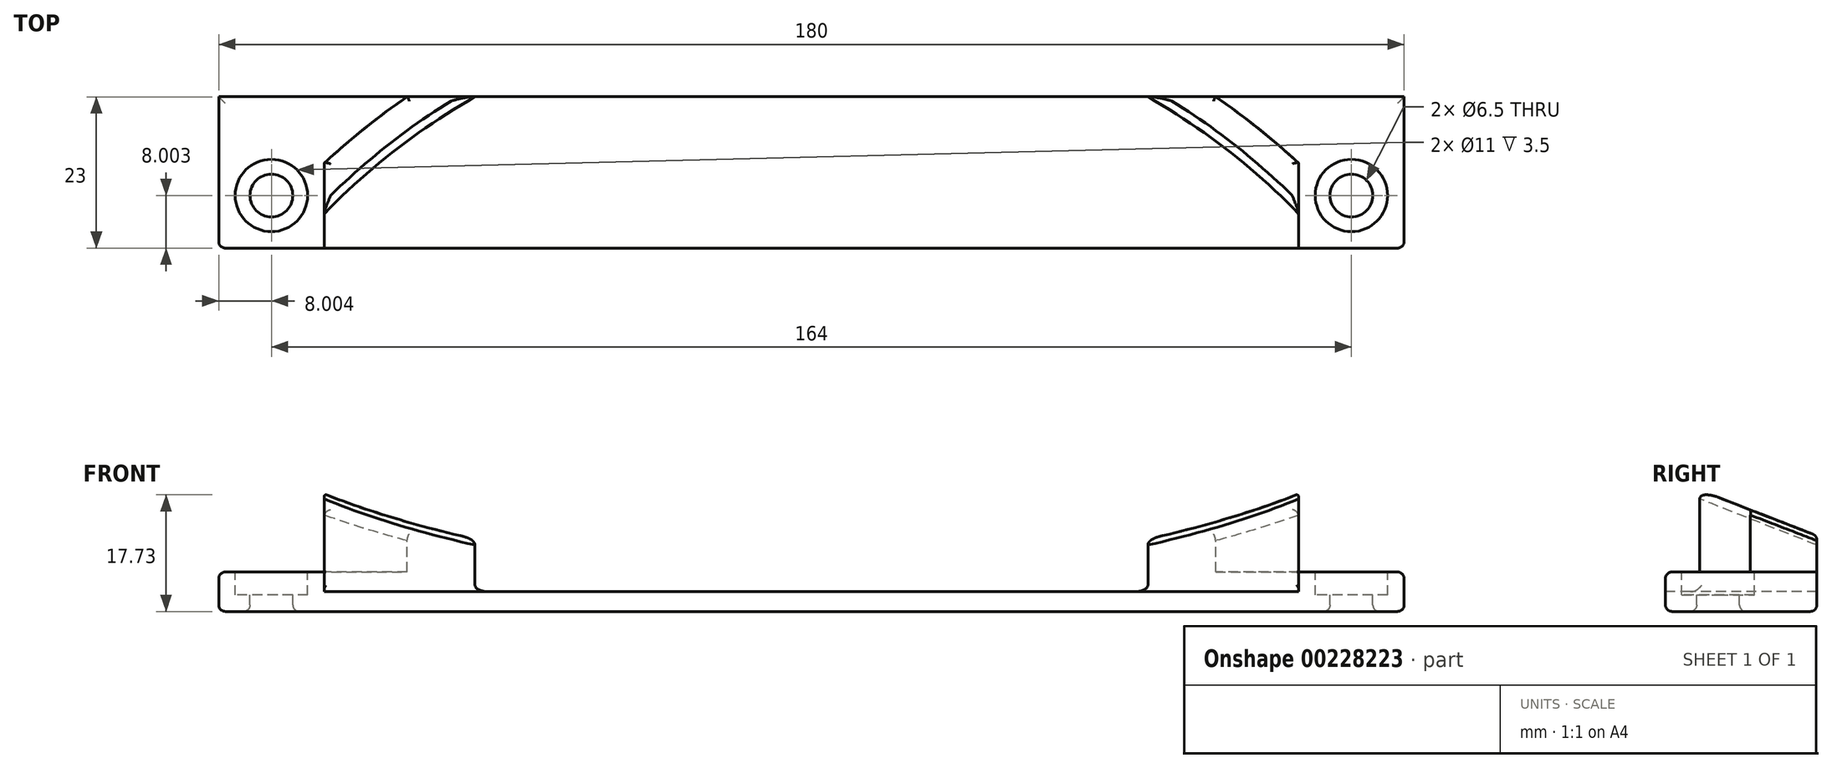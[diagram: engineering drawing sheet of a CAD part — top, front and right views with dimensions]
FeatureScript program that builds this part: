
annotation { "Feature Type Name" : "Feature", "Feature Type Description" : "" }
export const myFeature = defineFeature(function(context is Context, id is Id, definition is map)
    precondition{}
    {
        {
            var Q0;
            Q0=qCreatedBy(makeId("Top.planeOp"),FACE);
            var sketch = newSketch(context, id + "F0", { "sketchPlane" : qUnion([Q0])});
            skLineSegment(sketch, "E0.bottom", {"start": v(-72.48, -7.14) * mm, "end": v(107.52, -7.14) * mm});
            skLineSegment(sketch, "E0.top", {"start": v(-72.48, -30.14) * mm, "end": v(107.52, -30.14) * mm});
            skLineSegment(sketch, "E0.left", {"start": v(-72.48, -7.14) * mm, "end": v(-72.48, -30.14) * mm});
            skLineSegment(sketch, "E0.right", {"start": v(107.52, -7.14) * mm, "end": v(107.52, -30.14) * mm});
            skPoint(sketch, "E1", {"position": v(-64.48, -22.14) * mm});
            skPoint(sketch, "E2", {"position": v(99.52, -22.14) * mm});
            skSolve(sketch);
        }
        {
            var Q0;
            Q0=makeQuery(id+"F0.imprint","IMPRINT",FACE,{"disambiguationData":[TD([[makeQuery(id+"F0.imprint","IMPRINT",EDGE,{"derivedFrom":sQuery(id+"F0.wireOp",EDGE,"E0.bottom")}),-1.0]])]});
            extrude(context, id + "F1", {"entities" : qUnion([Q0]), "depth" : 6 * mm});
        }
        {
            var Q0;
            Q0=makeQuery(id+"F1.opExtrude","CAP_FACE",FACE,{"disambiguationData":[OSD([sQuery(id+"F0.wireOp",EDGE,"E0.bottom"),sQuery(id+"F0.wireOp",EDGE,"E0.top"),sQuery(id+"F0.wireOp",EDGE,"E0.left"),sQuery(id+"F0.wireOp",EDGE,"E0.right")])],"isStart":false});
            var sketch = newSketch(context, id + "F2", { "sketchPlane" : qUnion([Q0])});
            skPoint(sketch, "E3", {"position": v(-64.48, -22.14) * mm});
            skPoint(sketch, "E4", {"position": v(99.52, -22.14) * mm});
            skLineSegment(sketch, "E5.bottom", {"start": v(-56.48, -7.14) * mm, "end": v(91.52, -7.14) * mm});
            skLineSegment(sketch, "E5.top", {"start": v(-56.48, -30.14) * mm, "end": v(91.52, -30.14) * mm});
            skLineSegment(sketch, "E5.left", {"start": v(-56.48, -7.14) * mm, "end": v(-56.48, -30.14) * mm});
            skLineSegment(sketch, "E5.right", {"start": v(91.52, -7.14) * mm, "end": v(91.52, -30.14) * mm});
            skSolve(sketch);
        }
        {
            var Q0;
            Q0=sQuery(id+"F2.wireOp",VERTEX,"E3");
            var Q1;
            Q1=sQuery(id+"F2.wireOp",VERTEX,"E4");
            var Q2;
            Q2=makeQuery(id+"F1.opExtrude","SWEPT_BODY",BODY,{"disambiguationData":[OSD([sQuery(id+"F0.wireOp",EDGE,"E0.bottom"),sQuery(id+"F0.wireOp",EDGE,"E0.top"),sQuery(id+"F0.wireOp",EDGE,"E0.left"),sQuery(id+"F0.wireOp",EDGE,"E0.right")])]});
            hole(context, id + "F3", {"style" : HoleStyle.C_BORE, "endStyle" : HoleEndStyle.THROUGH, "holeDiameter" : 6.5 * mm, "cBoreDiameter" : 11 * mm, "cBoreDepth" : 3.5 * mm, "startFromSketch" : true, "locations" : qUnion([Q0, Q1]), "scope" : qUnion([Q2]), "isTappedThrough" : true});
        }
        {
            var Q0;
            Q0=makeQuery(id+"F2.imprint","IMPRINT",FACE,{"disambiguationData":[TD([[makeQuery(id+"F2.imprint","IMPRINT",EDGE,{"derivedFrom":sQuery(id+"F2.wireOp",EDGE,"E5.bottom")}),-1.0]])]});
            extrude(context, id + "F4", {"entities" : qUnion([Q0]), "operationType" : NewBodyOperationType.ADD, "depth" : 14 * mm});
        }
        {
            var Q0;
            Q0=makeQuery(id+"F4.opExtrude","CAP_FACE",FACE,{"disambiguationData":[OSD([sQuery(id+"F2.wireOp",EDGE,"E5.bottom"),sQuery(id+"F2.wireOp",EDGE,"E5.top"),sQuery(id+"F2.wireOp",EDGE,"E5.left"),sQuery(id+"F2.wireOp",EDGE,"E5.right")])],"isStart":false});
            var sketch = newSketch(context, id + "F5", { "sketchPlane" : qUnion([Q0])});
            skPoint(sketch, "E6", {"position": v(17.52, 2.86) * mm});
            skCircle(sketch, "E7", {"center": v(17.52, -96.6) * mm, "radius": 108.5 * mm});
            skCircle(sketch, "E8", {"center": v(17.52, -96.6) * mm, "radius": 103.03 * mm});
            skSolve(sketch);
        }
        {
            var Q0;
            {var subQ1=makeQuery(id+"F4.opExtrude","CAP_EDGE",EDGE,{"disambiguationData":[OSD([sQuery(id+"F2.wireOp",EDGE,"E5.top")])],"isStart":false});Q0=makeQuery(id+"F5.imprint","IMPRINT",FACE,{"disambiguationData":[TD([[makeQuery(id+"F5.imprint","IMPRINT",EDGE,{"derivedFrom":subQ1}),1.0]])]});}
            extrude(context, id + "F6", {"entities" : qUnion([Q0]), "operationType" : NewBodyOperationType.REMOVE, "oppositeDirection" : true, "depth" : 17 * mm});
        }
        {
            var Q0;
            {var subQ0=sQuery(id+"F5.wireOp",EDGE,"E7");var subQ1=makeQuery(id+"F4.opExtrude","CAP_EDGE",EDGE,{"disambiguationData":[OSD([sQuery(id+"F2.wireOp",EDGE,"E5.bottom")])],"isStart":false});var subQ2=makeQuery(id+"F5.imprint","INTERSECT",VERTEX,{"disambiguationData":[OD(1.0)],"derivedFrom":[subQ1,subQ0]});Q0=makeQuery(id+"F5.imprint","IMPRINT",FACE,{"disambiguationData":[TD([[makeQuery(id+"F5.imprint","IMPRINT",EDGE,{"disambiguationData":[TD([[subQ2,-1.0]])],"derivedFrom":subQ0}),-1.0]])]});}
            var Q1;
            {var subQ0=sQuery(id+"F5.wireOp",EDGE,"E7");var subQ1=makeQuery(id+"F4.opExtrude","CAP_EDGE",EDGE,{"disambiguationData":[OSD([sQuery(id+"F2.wireOp",EDGE,"E5.bottom")])],"isStart":false});var subQ2=makeQuery(id+"F5.imprint","INTERSECT",VERTEX,{"disambiguationData":[OD(0.0)],"derivedFrom":[subQ1,subQ0]});Q1=makeQuery(id+"F5.imprint","IMPRINT",FACE,{"disambiguationData":[TD([[makeQuery(id+"F5.imprint","IMPRINT",EDGE,{"disambiguationData":[TD([[subQ2,1.0]])],"derivedFrom":subQ0}),-1.0]])]});}
            extrude(context, id + "F7", {"entities" : qUnion([Q0, Q1]), "operationType" : NewBodyOperationType.REMOVE, "oppositeDirection" : true, "depth" : 14 * mm});
        }
        {
            var Q0;
            Q0=makeQuery(id+"F1.opExtrude","SWEPT_FACE",FACE,{"disambiguationData":[OSD([sQuery(id+"F0.wireOp",EDGE,"E0.right")])]});
            var sketch = newSketch(context, id + "F8", { "sketchPlane" : qUnion([Q0])});
            skLineSegment(sketch, "E9", {"start": v(-29.85, 20.35) * mm, "end": v(-5.4, 10.83) * mm});
            skLineSegment(sketch, "E10", {"start": v(-5.4, 10.83) * mm, "end": v(-5.4, 21.47) * mm});
            skLineSegment(sketch, "E11", {"start": v(-5.4, 21.47) * mm, "end": v(-29.85, 20.35) * mm});
            skSolve(sketch);
        }
        {
            var Q0;
            Q0=makeQuery(id+"F8.imprint","IMPRINT",FACE,{"disambiguationData":[TD([[makeQuery(id+"F8.imprint","IMPRINT",EDGE,{"derivedFrom":sQuery(id+"F8.wireOp",EDGE,"E9")}),1.0]])]});
            extrude(context, id + "F9", {"entities" : qUnion([Q0]), "operationType" : NewBodyOperationType.REMOVE, "oppositeDirection" : true, "depth" : 200 * mm});
        }
        {
            var Q0;
            {var subQ0=sQuery(id+"F2.wireOp",EDGE,"E5.right");Q0=makeQuery(id+"F9.boolean.opBoolean","COPY",FACE,{"disambiguationData":[TD([makeQuery(id+"F4.opExtrude","SWEPT_FACE",FACE,{"disambiguationData":[OSD([subQ0])]})])],"derivedFrom":makeQuery(id+"F9.opExtrude","SWEPT_FACE",FACE,{"disambiguationData":[OSD([sQuery(id+"F25IUwD2cY2oAvL_1.wireOp",EDGE,"SbL0lGDD-A6Ls-py6w-HqPT-BCFnm7Rx5yUF")])]})});}
            var Q1;
            {var subQ0=sQuery(id+"F2.wireOp",EDGE,"E5.left");Q1=makeQuery(id+"F9.boolean.opBoolean","COPY",FACE,{"disambiguationData":[TD([makeQuery(id+"F4.opExtrude","SWEPT_FACE",FACE,{"disambiguationData":[OSD([subQ0])]})])],"derivedFrom":makeQuery(id+"F9.opExtrude","SWEPT_FACE",FACE,{"disambiguationData":[OSD([sQuery(id+"F25IUwD2cY2oAvL_1.wireOp",EDGE,"SbL0lGDD-A6Ls-py6w-HqPT-BCFnm7Rx5yUF")])]})});}
            var Q2;
            Q2=makeQuery(id+"F6.boolean.opBoolean","COPY",EDGE,{"derivedFrom":makeQuery(id+"F6.opExtrude","CAP_EDGE",EDGE,{"disambiguationData":[OSD([sQuery(id+"F2.wireOp",EDGE,"E5.bottom")])],"isStart":false})});
            var Q3;
            Q3=makeQuery(id+"F6.boolean.opBoolean","COPY",EDGE,{"derivedFrom":makeQuery(id+"F6.opExtrude","CAP_EDGE",EDGE,{"disambiguationData":[OSD([sQuery(id+"F2.wireOp",EDGE,"E5.top")])],"isStart":false})});
            var Q4;
            {var subQ0=sQuery(id+"F0.wireOp",EDGE,"E0.right");var subQ1=sQuery(id+"F0.wireOp",EDGE,"E0.top");Q4=makeQuery(id+"F4.boolean.opBoolean","SPLIT",EDGE,{"disambiguationData":[TD([makeQuery(id+"F1.opExtrude","SWEPT_FACE",FACE,{"disambiguationData":[OSD([subQ0])]})])],"derivedFrom":makeQuery(id+"F1.opExtrude","CAP_EDGE",EDGE,{"disambiguationData":[OSD([subQ1])],"isStart":false})});}
            var Q5;
            Q5=makeQuery(id+"F1.opExtrude","CAP_EDGE",EDGE,{"disambiguationData":[OSD([sQuery(id+"F0.wireOp",EDGE,"E0.right")])],"isStart":false});
            var Q6;
            {var subQ0=sQuery(id+"F2.wireOp",EDGE,"E5.right");var subQ1=sQuery(id+"F2.wireOp",EDGE,"E5.bottom");var subQ2=makeQuery(id+"F4.opExtrude","CAP_EDGE",EDGE,{"disambiguationData":[OSD([subQ1])],"isStart":false});var subQ3=sQuery(id+"F0.wireOp",EDGE,"E0.right");var subQ4=sQuery(id+"F0.wireOp",EDGE,"E0.bottom");Q6=makeQuery(id+"F7.boolean.opBoolean","MERGE",EDGE,{"derivedFrom":[makeQuery(id+"F4.boolean.opBoolean","SPLIT",EDGE,{"disambiguationData":[TD([makeQuery(id+"F1.opExtrude","SWEPT_FACE",FACE,{"disambiguationData":[OSD([subQ3])]})])],"derivedFrom":makeQuery(id+"F1.opExtrude","CAP_EDGE",EDGE,{"disambiguationData":[OSD([subQ4])],"isStart":false})}),makeQuery(id+"F7.opExtrude","CAP_EDGE",EDGE,{"disambiguationData":[OSD([subQ1]),TDD([makeQuery(id+"F5.imprint","IMPRINT",EDGE,{"disambiguationData":[TD([[makeQuery(id+"F5.imprint","INTERSECT",VERTEX,{"derivedFrom":[subQ2,makeQuery(id+"F4.opExtrude","CAP_EDGE",EDGE,{"disambiguationData":[OSD([subQ0])],"isStart":false})]}),1.0]])],"derivedFrom":subQ2})])],"isStart":false})]});}
            var Q7;
            Q7=makeQuery(id+"F3.hole-1.boolean.opBoolean","COPY",EDGE,{"derivedFrom":makeQuery(id+"F3.hole-1.opRevolve","SWEPT_EDGE",EDGE,{"disambiguationData":[OSD([sQuery(id+"F3.hole-1.sketch.wireOp",EDGE,"cbore_start_line_2"),sQuery(id+"F3.hole-1.sketch.wireOp",EDGE,"cbore_start_line_3")])]})});
            var Q8;
            Q8=makeQuery(id+"F3.hole-1.boolean.opBoolean","COPY",EDGE,{"derivedFrom":makeQuery(id+"F3.hole-1.opRevolve","SWEPT_EDGE",EDGE,{"disambiguationData":[OSD([sQuery(id+"F3.hole-1.sketch.wireOp",EDGE,"cbore_start_line_1"),sQuery(id+"F3.hole-1.sketch.wireOp",EDGE,"core_line_2")])]})});
            var Q9;
            Q9=makeQuery(id+"F3.hole-0.boolean.opBoolean","COPY",EDGE,{"derivedFrom":makeQuery(id+"F3.hole-0.opRevolve","SWEPT_EDGE",EDGE,{"disambiguationData":[OSD([sQuery(id+"F3.hole-0.sketch.wireOp",EDGE,"cbore_start_line_1"),sQuery(id+"F3.hole-0.sketch.wireOp",EDGE,"core_line_2")])]})});
            var Q10;
            Q10=makeQuery(id+"F3.hole-0.boolean.opBoolean","COPY",EDGE,{"derivedFrom":makeQuery(id+"F3.hole-0.opRevolve","SWEPT_EDGE",EDGE,{"disambiguationData":[OSD([sQuery(id+"F3.hole-0.sketch.wireOp",EDGE,"cbore_start_line_2"),sQuery(id+"F3.hole-0.sketch.wireOp",EDGE,"cbore_start_line_3")])]})});
            var Q11;
            {var subQ0=sQuery(id+"F0.wireOp",EDGE,"E0.left");var subQ1=sQuery(id+"F0.wireOp",EDGE,"E0.top");Q11=makeQuery(id+"F4.boolean.opBoolean","SPLIT",EDGE,{"disambiguationData":[TD([makeQuery(id+"F1.opExtrude","SWEPT_FACE",FACE,{"disambiguationData":[OSD([subQ0])]})])],"derivedFrom":makeQuery(id+"F1.opExtrude","CAP_EDGE",EDGE,{"disambiguationData":[OSD([subQ1])],"isStart":false})});}
            var Q12;
            Q12=makeQuery(id+"F1.opExtrude","CAP_EDGE",EDGE,{"disambiguationData":[OSD([sQuery(id+"F0.wireOp",EDGE,"E0.left")])],"isStart":false});
            var Q13;
            {var subQ0=sQuery(id+"F2.wireOp",EDGE,"E5.left");var subQ1=sQuery(id+"F2.wireOp",EDGE,"E5.bottom");var subQ2=makeQuery(id+"F4.opExtrude","CAP_EDGE",EDGE,{"disambiguationData":[OSD([subQ1])],"isStart":false});var subQ3=sQuery(id+"F0.wireOp",EDGE,"E0.left");var subQ4=sQuery(id+"F0.wireOp",EDGE,"E0.bottom");Q13=makeQuery(id+"F7.boolean.opBoolean","MERGE",EDGE,{"derivedFrom":[makeQuery(id+"F4.boolean.opBoolean","SPLIT",EDGE,{"disambiguationData":[TD([makeQuery(id+"F1.opExtrude","SWEPT_FACE",FACE,{"disambiguationData":[OSD([subQ3])]})])],"derivedFrom":makeQuery(id+"F1.opExtrude","CAP_EDGE",EDGE,{"disambiguationData":[OSD([subQ4])],"isStart":false})}),makeQuery(id+"F7.opExtrude","CAP_EDGE",EDGE,{"disambiguationData":[OSD([subQ1]),TDD([makeQuery(id+"F5.imprint","IMPRINT",EDGE,{"disambiguationData":[TD([[makeQuery(id+"F5.imprint","INTERSECT",VERTEX,{"derivedFrom":[subQ2,makeQuery(id+"F4.opExtrude","CAP_EDGE",EDGE,{"disambiguationData":[OSD([subQ0])],"isStart":false})]}),-1.0]])],"derivedFrom":subQ2})])],"isStart":false})]});}
            var Q14;
            Q14=makeQuery(id+"F1.opExtrude","CAP_EDGE",EDGE,{"disambiguationData":[OSD([sQuery(id+"F0.wireOp",EDGE,"E0.bottom")])],"isStart":true});
            var Q15;
            Q15=makeQuery(id+"F1.opExtrude","CAP_EDGE",EDGE,{"disambiguationData":[OSD([sQuery(id+"F0.wireOp",EDGE,"E0.top")])],"isStart":true});
            var Q16;
            Q16=makeQuery(id+"F1.opExtrude","CAP_EDGE",EDGE,{"disambiguationData":[OSD([sQuery(id+"F0.wireOp",EDGE,"E0.right")])],"isStart":true});
            var Q17;
            Q17=makeQuery(id+"F1.opExtrude","CAP_EDGE",EDGE,{"disambiguationData":[OSD([sQuery(id+"F0.wireOp",EDGE,"E0.left")])],"isStart":true});
            var Q18;
            Q18=makeQuery(id+"F1.opExtrude","CAP_FACE",FACE,{"disambiguationData":[OSD([sQuery(id+"F0.wireOp",EDGE,"E0.bottom"),sQuery(id+"F0.wireOp",EDGE,"E0.top"),sQuery(id+"F0.wireOp",EDGE,"E0.left"),sQuery(id+"F0.wireOp",EDGE,"E0.right")])],"isStart":true});
            var Q19;
            Q19=makeQuery(id+"F3.hole-0.boolean.opBoolean","INTERSECT",EDGE,{"derivedFrom":[makeQuery(id+"F1.opExtrude","CAP_FACE",FACE,{"disambiguationData":[OSD([sQuery(id+"F0.wireOp",EDGE,"E0.bottom"),sQuery(id+"F0.wireOp",EDGE,"E0.top"),sQuery(id+"F0.wireOp",EDGE,"E0.left"),sQuery(id+"F0.wireOp",EDGE,"E0.right")])],"isStart":true}),makeQuery(id+"F3.hole-0.opRevolve","SWEPT_FACE",FACE,{"disambiguationData":[OSD([sQuery(id+"F3.hole-0.sketch.wireOp",EDGE,"core_line_2")])]})]});
            var Q20;
            Q20=makeQuery(id+"F7.boolean.opBoolean","COPY",EDGE,{"derivedFrom":makeQuery(id+"F7.opExtrude","SWEPT_EDGE",EDGE,{"disambiguationData":[OSD([sQuery(id+"F2.wireOp",EDGE,"E5.left"),sQuery(id+"F5.wireOp",EDGE,"E7")])]})});
            var Q21;
            {var subQ0=sQuery(id+"F5.wireOp",EDGE,"E7");var subQ1=sQuery(id+"F2.wireOp",EDGE,"E5.bottom");Q21=makeQuery(id+"F7.boolean.opBoolean","COPY",EDGE,{"derivedFrom":makeQuery(id+"F7.opExtrude","SWEPT_EDGE",EDGE,{"disambiguationData":[OSD([subQ1,subQ0]),TDD([makeQuery(id+"F5.imprint","INTERSECT",VERTEX,{"disambiguationData":[OD(1.0)],"derivedFrom":[makeQuery(id+"F4.opExtrude","CAP_EDGE",EDGE,{"disambiguationData":[OSD([subQ1])],"isStart":false}),subQ0]})])]})});}
            var Q22;
            Q22=makeQuery(id+"F7.boolean.opBoolean","COPY",EDGE,{"derivedFrom":makeQuery(id+"F7.opExtrude","SWEPT_EDGE",EDGE,{"disambiguationData":[OSD([sQuery(id+"F2.wireOp",EDGE,"E5.right"),sQuery(id+"F5.wireOp",EDGE,"E7")])]})});
            var Q23;
            {var subQ0=sQuery(id+"F5.wireOp",EDGE,"E8");Q23=makeQuery(id+"F9.boolean.opBoolean","INTERSECT",EDGE,{"derivedFrom":[makeQuery(id+"F6.boolean.opBoolean","COPY",FACE,{"derivedFrom":makeQuery(id+"F6.opExtrude","SWEPT_FACE",FACE,{"disambiguationData":[OSD([subQ0]),TDD([makeQuery(id+"F5.imprint","IMPRINT",EDGE,{"disambiguationData":[TD([[makeQuery(id+"F5.imprint","INTERSECT",VERTEX,{"disambiguationData":[OD(0.0)],"derivedFrom":[makeQuery(id+"F4.opExtrude","CAP_EDGE",EDGE,{"disambiguationData":[OSD([sQuery(id+"F2.wireOp",EDGE,"E5.bottom")])],"isStart":false}),subQ0]}),1.0]])],"derivedFrom":subQ0})])]})}),makeQuery(id+"F9.opExtrude","SWEPT_FACE",FACE,{"disambiguationData":[OSD([sQuery(id+"F8.wireOp",EDGE,"E9")])]})]});}
            var Q24;
            {var subQ0=sQuery(id+"F5.wireOp",EDGE,"E7");Q24=makeQuery(id+"F9.boolean.opBoolean","INTERSECT",EDGE,{"derivedFrom":[makeQuery(id+"F7.boolean.opBoolean","COPY",FACE,{"derivedFrom":makeQuery(id+"F7.opExtrude","SWEPT_FACE",FACE,{"disambiguationData":[OSD([subQ0]),TDD([makeQuery(id+"F5.imprint","IMPRINT",EDGE,{"disambiguationData":[TD([[makeQuery(id+"F5.imprint","INTERSECT",VERTEX,{"disambiguationData":[OD(0.0)],"derivedFrom":[makeQuery(id+"F4.opExtrude","CAP_EDGE",EDGE,{"disambiguationData":[OSD([sQuery(id+"F2.wireOp",EDGE,"E5.bottom")])],"isStart":false}),subQ0]}),1.0]])],"derivedFrom":subQ0})])]})}),makeQuery(id+"F9.opExtrude","SWEPT_FACE",FACE,{"disambiguationData":[OSD([sQuery(id+"F8.wireOp",EDGE,"E9")])]})]});}
            var Q25;
            Q25=makeQuery(id+"F9.boolean.opBoolean","INTERSECT",EDGE,{"disambiguationData":[OD(0.0)],"derivedFrom":[makeQuery(id+"F4.boolean.opBoolean","MERGE",FACE,{"derivedFrom":[makeQuery(id+"F1.opExtrude","SWEPT_FACE",FACE,{"disambiguationData":[OSD([sQuery(id+"F0.wireOp",EDGE,"E0.bottom")])]}),makeQuery(id+"F4.opExtrude","SWEPT_FACE",FACE,{"disambiguationData":[OSD([sQuery(id+"F2.wireOp",EDGE,"E5.bottom")])]})]}),makeQuery(id+"F9.opExtrude","SWEPT_FACE",FACE,{"disambiguationData":[OSD([sQuery(id+"F8.wireOp",EDGE,"E9")])]})]});
            var Q26;
            Q26=makeQuery(id+"F9.boolean.opBoolean","INTERSECT",EDGE,{"derivedFrom":[makeQuery(id+"F4.opExtrude","SWEPT_FACE",FACE,{"disambiguationData":[OSD([sQuery(id+"F2.wireOp",EDGE,"E5.right")])]}),makeQuery(id+"F9.opExtrude","SWEPT_FACE",FACE,{"disambiguationData":[OSD([sQuery(id+"F8.wireOp",EDGE,"E9")])]})]});
            var Q27;
            {var subQ0=sQuery(id+"F2.wireOp",EDGE,"E5.right");var subQ1=sQuery(id+"F2.wireOp",EDGE,"E5.bottom");var subQ2=sQuery(id+"F5.wireOp",EDGE,"E8");Q27=makeQuery(id+"F6.boolean.opBoolean","COPY",EDGE,{"disambiguationData":[TD([makeQuery(id+"F4.opExtrude","CAP_FACE",FACE,{"disambiguationData":[OSD([subQ1,sQuery(id+"F2.wireOp",EDGE,"E5.top"),sQuery(id+"F2.wireOp",EDGE,"E5.left"),subQ0])],"isStart":false})])],"derivedFrom":makeQuery(id+"F6.opExtrude","SWEPT_EDGE",EDGE,{"disambiguationData":[OSD([subQ0,subQ2])]})});}
            var Q28;
            {var subQ0=sQuery(id+"F5.wireOp",EDGE,"E7");Q28=makeQuery(id+"F9.boolean.opBoolean","INTERSECT",EDGE,{"derivedFrom":[makeQuery(id+"F7.boolean.opBoolean","COPY",FACE,{"derivedFrom":makeQuery(id+"F7.opExtrude","SWEPT_FACE",FACE,{"disambiguationData":[OSD([subQ0]),TDD([makeQuery(id+"F5.imprint","IMPRINT",EDGE,{"disambiguationData":[TD([[makeQuery(id+"F5.imprint","INTERSECT",VERTEX,{"disambiguationData":[OD(1.0)],"derivedFrom":[makeQuery(id+"F4.opExtrude","CAP_EDGE",EDGE,{"disambiguationData":[OSD([sQuery(id+"F2.wireOp",EDGE,"E5.bottom")])],"isStart":false}),subQ0]}),-1.0]])],"derivedFrom":subQ0})])]})}),makeQuery(id+"F9.opExtrude","SWEPT_FACE",FACE,{"disambiguationData":[OSD([sQuery(id+"F8.wireOp",EDGE,"E9")])]})]});}
            var Q29;
            Q29=makeQuery(id+"F9.boolean.opBoolean","INTERSECT",EDGE,{"disambiguationData":[OD(1.0)],"derivedFrom":[makeQuery(id+"F4.boolean.opBoolean","MERGE",FACE,{"derivedFrom":[makeQuery(id+"F1.opExtrude","SWEPT_FACE",FACE,{"disambiguationData":[OSD([sQuery(id+"F0.wireOp",EDGE,"E0.bottom")])]}),makeQuery(id+"F4.opExtrude","SWEPT_FACE",FACE,{"disambiguationData":[OSD([sQuery(id+"F2.wireOp",EDGE,"E5.bottom")])]})]}),makeQuery(id+"F9.opExtrude","SWEPT_FACE",FACE,{"disambiguationData":[OSD([sQuery(id+"F8.wireOp",EDGE,"E9")])]})]});
            var Q30;
            Q30=makeQuery(id+"F9.boolean.opBoolean","INTERSECT",EDGE,{"derivedFrom":[makeQuery(id+"F4.opExtrude","SWEPT_FACE",FACE,{"disambiguationData":[OSD([sQuery(id+"F2.wireOp",EDGE,"E5.left")])]}),makeQuery(id+"F9.opExtrude","SWEPT_FACE",FACE,{"disambiguationData":[OSD([sQuery(id+"F8.wireOp",EDGE,"E9")])]})]});
            var Q31;
            {var subQ0=sQuery(id+"F5.wireOp",EDGE,"E8");var subQ1=sQuery(id+"F2.wireOp",EDGE,"E5.bottom");var subQ2=sQuery(id+"F2.wireOp",EDGE,"E5.left");Q31=makeQuery(id+"F6.boolean.opBoolean","COPY",EDGE,{"disambiguationData":[TD([makeQuery(id+"F4.opExtrude","CAP_FACE",FACE,{"disambiguationData":[OSD([subQ1,sQuery(id+"F2.wireOp",EDGE,"E5.top"),subQ2,sQuery(id+"F2.wireOp",EDGE,"E5.right")])],"isStart":false})])],"derivedFrom":makeQuery(id+"F6.opExtrude","SWEPT_EDGE",EDGE,{"disambiguationData":[OSD([subQ2,subQ0])]})});}
            var Q32;
            {var subQ0=sQuery(id+"F5.wireOp",EDGE,"E8");var subQ1=sQuery(id+"F2.wireOp",EDGE,"E5.bottom");Q32=makeQuery(id+"F6.boolean.opBoolean","COPY",EDGE,{"derivedFrom":makeQuery(id+"F6.opExtrude","SWEPT_EDGE",EDGE,{"disambiguationData":[OSD([subQ1,subQ0]),TDD([makeQuery(id+"F5.imprint","INTERSECT",VERTEX,{"disambiguationData":[OD(0.0)],"derivedFrom":[makeQuery(id+"F4.opExtrude","CAP_EDGE",EDGE,{"disambiguationData":[OSD([subQ1])],"isStart":false}),subQ0]})])]})});}
            var Q33;
            {var subQ0=sQuery(id+"F5.wireOp",EDGE,"E8");var subQ1=sQuery(id+"F2.wireOp",EDGE,"E5.bottom");Q33=makeQuery(id+"F6.boolean.opBoolean","COPY",EDGE,{"derivedFrom":makeQuery(id+"F6.opExtrude","SWEPT_EDGE",EDGE,{"disambiguationData":[OSD([subQ1,subQ0]),TDD([makeQuery(id+"F5.imprint","INTERSECT",VERTEX,{"disambiguationData":[OD(1.0)],"derivedFrom":[makeQuery(id+"F4.opExtrude","CAP_EDGE",EDGE,{"disambiguationData":[OSD([subQ1])],"isStart":false}),subQ0]})])]})});}
            var Q34;
            {var subQ0=sQuery(id+"F5.wireOp",EDGE,"E8");Q34=makeQuery(id+"F6.boolean.opBoolean","COPY",EDGE,{"derivedFrom":makeQuery(id+"F6.opExtrude","CAP_EDGE",EDGE,{"disambiguationData":[OSD([subQ0]),TDD([makeQuery(id+"F5.imprint","IMPRINT",EDGE,{"disambiguationData":[TD([[makeQuery(id+"F5.imprint","INTERSECT",VERTEX,{"disambiguationData":[OD(0.0)],"derivedFrom":[makeQuery(id+"F4.opExtrude","CAP_EDGE",EDGE,{"disambiguationData":[OSD([sQuery(id+"F2.wireOp",EDGE,"E5.bottom")])],"isStart":false}),subQ0]}),1.0]])],"derivedFrom":subQ0})])],"isStart":false})});}
            var Q35;
            {var subQ0=sQuery(id+"F5.wireOp",EDGE,"E8");Q35=makeQuery(id+"F9.boolean.opBoolean","INTERSECT",EDGE,{"derivedFrom":[makeQuery(id+"F6.boolean.opBoolean","COPY",FACE,{"derivedFrom":makeQuery(id+"F6.opExtrude","SWEPT_FACE",FACE,{"disambiguationData":[OSD([subQ0]),TDD([makeQuery(id+"F5.imprint","IMPRINT",EDGE,{"disambiguationData":[TD([[makeQuery(id+"F5.imprint","INTERSECT",VERTEX,{"disambiguationData":[OD(1.0)],"derivedFrom":[makeQuery(id+"F4.opExtrude","CAP_EDGE",EDGE,{"disambiguationData":[OSD([sQuery(id+"F2.wireOp",EDGE,"E5.bottom")])],"isStart":false}),subQ0]}),-1.0]])],"derivedFrom":subQ0})])]})}),makeQuery(id+"F9.opExtrude","SWEPT_FACE",FACE,{"disambiguationData":[OSD([sQuery(id+"F8.wireOp",EDGE,"E9")])]})]});}
            var Q36;
            {var subQ0=sQuery(id+"F5.wireOp",EDGE,"E8");Q36=makeQuery(id+"F6.boolean.opBoolean","COPY",EDGE,{"derivedFrom":makeQuery(id+"F6.opExtrude","CAP_EDGE",EDGE,{"disambiguationData":[OSD([subQ0]),TDD([makeQuery(id+"F5.imprint","IMPRINT",EDGE,{"disambiguationData":[TD([[makeQuery(id+"F5.imprint","INTERSECT",VERTEX,{"disambiguationData":[OD(1.0)],"derivedFrom":[makeQuery(id+"F4.opExtrude","CAP_EDGE",EDGE,{"disambiguationData":[OSD([sQuery(id+"F2.wireOp",EDGE,"E5.bottom")])],"isStart":false}),subQ0]}),-1.0]])],"derivedFrom":subQ0})])],"isStart":false})});}
            var Q37;
            Q37=makeQuery(id+"F1.opExtrude","SWEPT_EDGE",EDGE,{"disambiguationData":[OSD([sQuery(id+"F0.wireOp",EDGE,"E0.top"),sQuery(id+"F0.wireOp",EDGE,"E0.right")])]});
            var Q38;
            Q38=makeQuery(id+"F1.opExtrude","SWEPT_EDGE",EDGE,{"disambiguationData":[OSD([sQuery(id+"F0.wireOp",EDGE,"E0.top"),sQuery(id+"F0.wireOp",EDGE,"E0.left")])]});
            fillet(context, id + "F10", {"entities" : qUnion([Q0, Q1, Q2, Q3, Q4, Q5, Q6, Q7, Q8, Q9, Q10, Q11, Q12, Q13, Q14, Q15, Q16, Q17, Q18, Q19, Q20, Q21, Q22, Q23, Q24, Q25, Q26, Q27, Q28, Q29, Q30, Q31, Q32, Q33, Q34, Q35, Q36, Q37, Q38]), "radius" : 1 * mm, "tangentPropagation" : true, "allowEdgeOverflow" : false});
        }
    });
